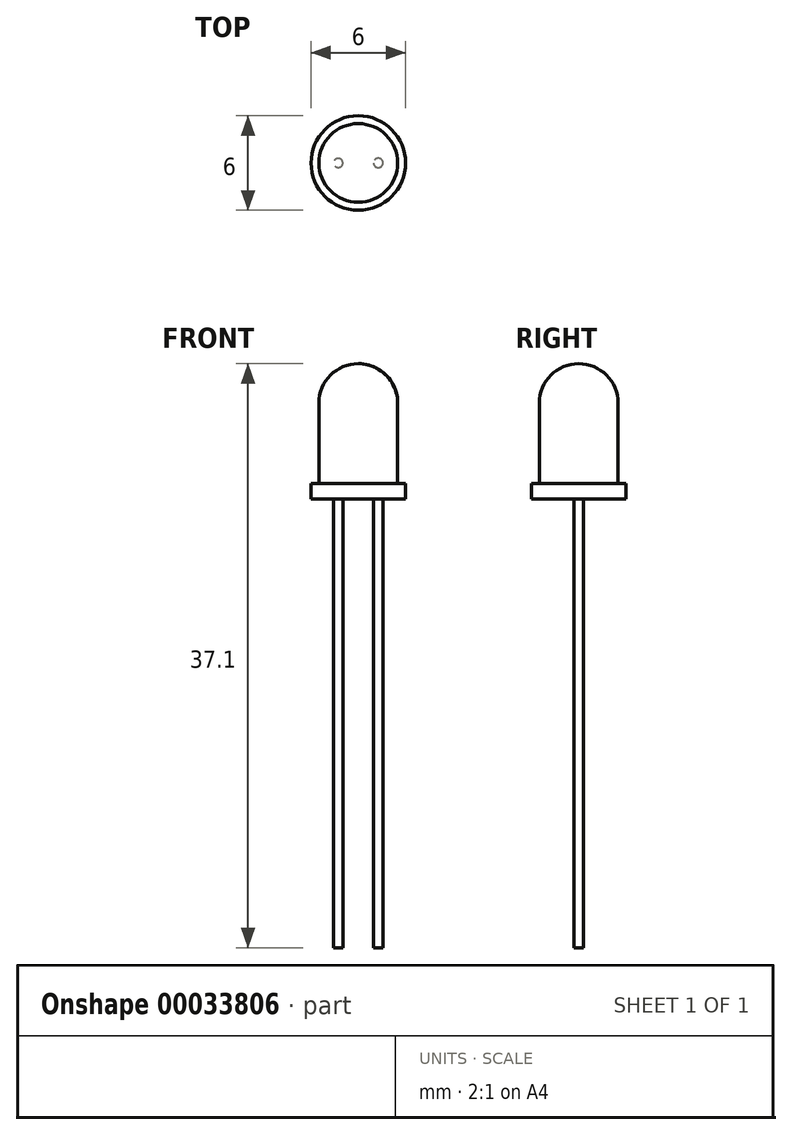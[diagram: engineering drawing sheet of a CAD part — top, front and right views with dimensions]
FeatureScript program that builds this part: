
annotation { "Feature Type Name" : "Feature", "Feature Type Description" : "" }
export const myFeature = defineFeature(function(context is Context, id is Id, definition is map)
    precondition{}
    {
        {
            var Q0;
            Q0=qCreatedBy(makeId("Front.planeOp"),FACE);
            var sketch = newSketch(context, id + "F0", { "sketchPlane" : qUnion([Q0])});
            skLineSegment(sketch, "E0", {"start": v(0, 0) * mm, "end": v(3, 0) * mm});
            skLineSegment(sketch, "E1", {"start": v(3, 0) * mm, "end": v(3, 1) * mm});
            skLineSegment(sketch, "E2", {"start": v(3, 1) * mm, "end": v(2.5, 1) * mm});
            skLineSegment(sketch, "E3", {"start": v(2.5, 1) * mm, "end": v(2.5, 6.1) * mm});
            skLineSegment(sketch, "E4", {"start": v(0, 8.6) * mm, "end": v(0, 8.6) * mm});
            skLineSegment(sketch, "E5", {"start": v(0, 8.6) * mm, "end": v(0, 0) * mm});
            skPoint(sketch, "E6.visualSharp", {"position": v(2.5, 8.6) * mm});
            skArc(sketch, "E6.filletArc", {"start": v(2.5, 6.1) * mm, "mid": v(1.77, 7.87) * mm, "end": v(0, 8.6) * mm});
            skSolve(sketch);
        }
        {
            var Q0;
            Q0=makeQuery(id+"F0.imprint","IMPRINT",FACE,{"disambiguationData":[TD([[makeQuery(id+"F0.imprint","IMPRINT",EDGE,{"derivedFrom":sQuery(id+"F0.wireOp",EDGE,"E0")}),1.0]])]});
            var Q1;
            Q1=sQuery(id+"F0.wireOp",EDGE,"E5");
            revolve(context, id + "F1", {"entities" : qUnion([Q0]), "axis" : qUnion([Q1]), "revolveType" : RevolveType.FULL});
        }
        {
            var Q0;
            Q0=makeQuery(id+"F1.opRevolve","SWEPT_FACE",FACE,{"disambiguationData":[OSD([sQuery(id+"F0.wireOp",EDGE,"E0")])]});
            var sketch = newSketch(context, id + "F2", { "sketchPlane" : qUnion([Q0])});
            skCircle(sketch, "E7", {"center": v(-1.27, 0) * mm, "radius": 0.29 * mm});
            skCircle(sketch, "E8", {"center": v(1.27, 0) * mm, "radius": 0.3 * mm});
            skSolve(sketch);
        }
        {
            var Q0;
            Q0=makeQuery(id+"F2.imprint","IMPRINT",FACE,{"disambiguationData":[TD([[makeQuery(id+"F2.imprint","IMPRINT",EDGE,{"derivedFrom":sQuery(id+"F2.wireOp",EDGE,"E8")}),1.0]])]});
            var Q1;
            Q1=makeQuery(id+"F2.imprint","IMPRINT",FACE,{"disambiguationData":[TD([[makeQuery(id+"F2.imprint","IMPRINT",EDGE,{"derivedFrom":sQuery(id+"F2.wireOp",EDGE,"E7")}),1.0]])]});
            extrude(context, id + "F3", {"entities" : qUnion([Q0, Q1]), "operationType" : NewBodyOperationType.ADD, "depth" : 28.5 * mm});
        }
    });
